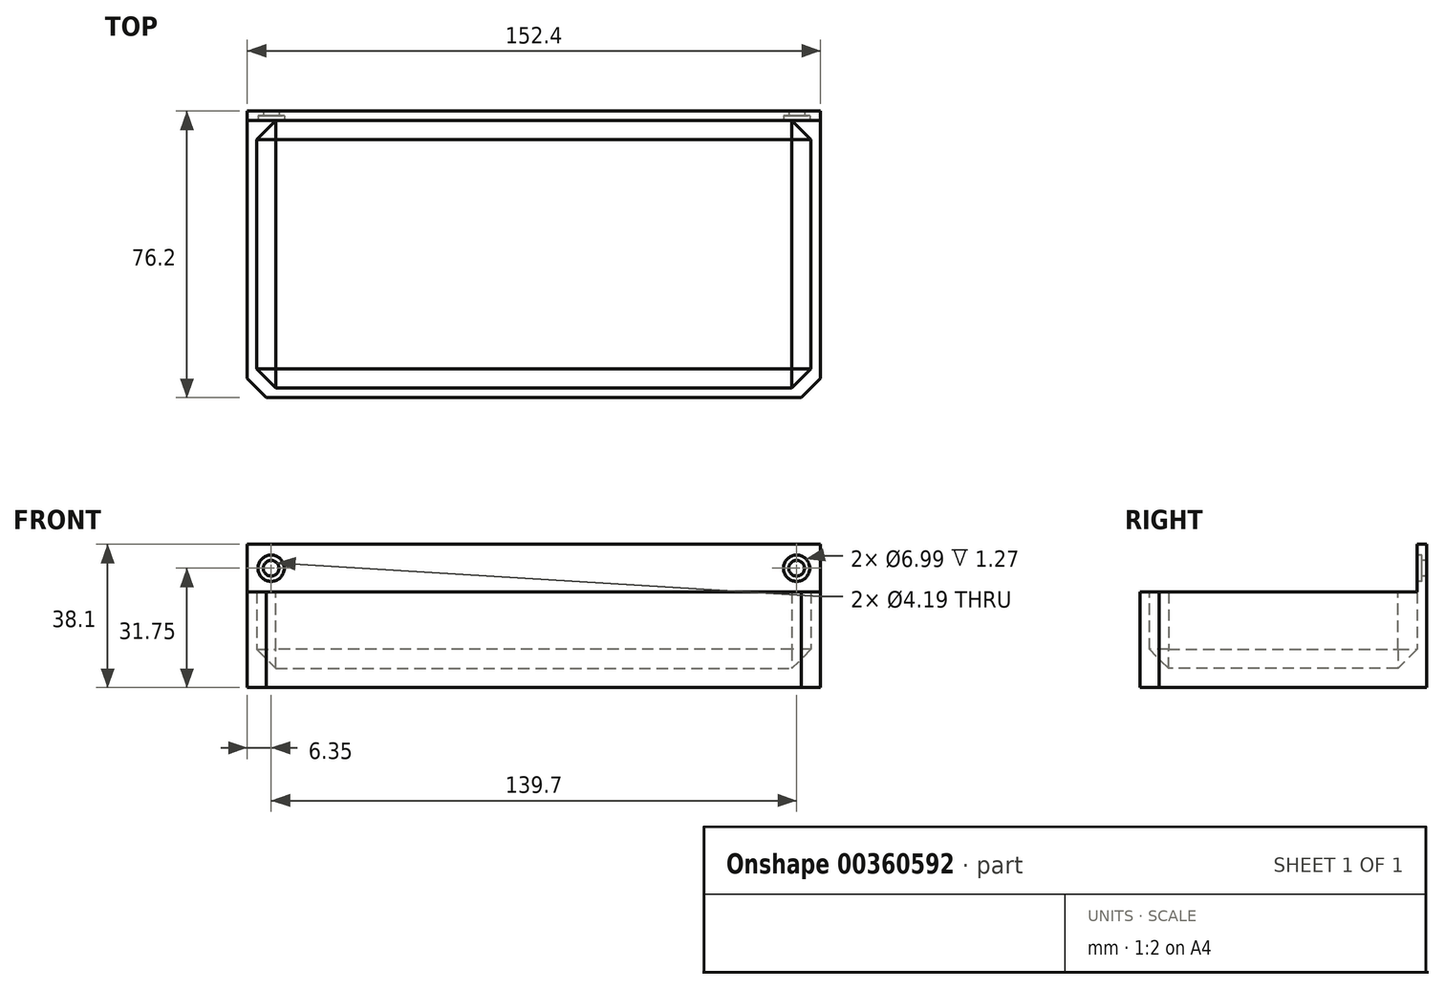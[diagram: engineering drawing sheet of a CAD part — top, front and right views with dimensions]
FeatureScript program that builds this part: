
annotation { "Feature Type Name" : "Feature", "Feature Type Description" : "" }
export const myFeature = defineFeature(function(context is Context, id is Id, definition is map)
    precondition{}
    {
        {
            var Q0;
            Q0=qCreatedBy(makeId("Top.planeOp"),FACE);
            var sketch = newSketch(context, id + "F0", { "sketchPlane" : qUnion([Q0])});
            skLineSegment(sketch, "E0.bottom", {"start": v(0, 0) * mm, "end": v(152.4, 0) * mm});
            skLineSegment(sketch, "E0.top", {"start": v(0, 76.2) * mm, "end": v(152.4, 76.2) * mm});
            skLineSegment(sketch, "E0.left", {"start": v(0, 0) * mm, "end": v(0, 76.2) * mm});
            skLineSegment(sketch, "E0.right", {"start": v(152.4, 0) * mm, "end": v(152.4, 76.2) * mm});
            skLineSegment(sketch, "E1.bottom", {"start": v(2.54, 2.54) * mm, "end": v(149.86, 2.54) * mm});
            skLineSegment(sketch, "E1.top", {"start": v(2.54, 73.66) * mm, "end": v(149.86, 73.66) * mm});
            skLineSegment(sketch, "E1.left", {"start": v(2.54, 2.54) * mm, "end": v(2.54, 73.66) * mm});
            skLineSegment(sketch, "E1.right", {"start": v(149.86, 2.54) * mm, "end": v(149.86, 73.66) * mm});
            skSolve(sketch);
        }
        {
            var Q0;
            Q0 = qSketchRegion(id + "F0", true);
            extrude(context, id + "F1", {"entities" : qUnion([Q0]), "depth" : 25.4 * mm});
        }
        {
            var Q0;
            Q0 = qSketchRegion(id + "F0", true);
            var Q1;
            Q1=makeQuery(id+"F0.imprint","IMPRINT",FACE,{"disambiguationData":[TD([[makeQuery(id+"F0.imprint","IMPRINT",EDGE,{"derivedFrom":sQuery(id+"F0.wireOp",EDGE,"E1.bottom")}),1.0]])]});
            extrude(context, id + "F2", {"entities" : qUnion([Q0, Q1]), "operationType" : NewBodyOperationType.ADD, "depth" : 5.08 * mm});
        }
        {
            var Q0;
            Q0=makeQuery(id+"F1.opExtrude","CAP_FACE",FACE,{"disambiguationData":[OSD([sQuery(id+"F0.wireOp",EDGE,"E0.bottom"),sQuery(id+"F0.wireOp",EDGE,"E0.top"),sQuery(id+"F0.wireOp",EDGE,"E0.left"),sQuery(id+"F0.wireOp",EDGE,"E0.right"),sQuery(id+"F0.wireOp",EDGE,"E1.bottom"),sQuery(id+"F0.wireOp",EDGE,"E1.top"),sQuery(id+"F0.wireOp",EDGE,"E1.left"),sQuery(id+"F0.wireOp",EDGE,"E1.right")])],"isStart":false});
            var sketch = newSketch(context, id + "F3", { "sketchPlane" : qUnion([Q0])});
            skLineSegment(sketch, "E2", {"start": v(0, 73.66) * mm, "end": v(152.4, 73.66) * mm});
            skSolve(sketch);
        }
        {
            var Q0;
            {var subQ0=makeQuery(id+"F1.opExtrude","CAP_EDGE",EDGE,{"disambiguationData":[OSD([sQuery(id+"F0.wireOp",EDGE,"E0.top")])],"isStart":false});Q0=makeQuery(id+"F3.imprint","IMPRINT",FACE,{"disambiguationData":[TD([[makeQuery(id+"F3.imprint","IMPRINT",EDGE,{"derivedFrom":subQ0}),-1.0]])]});}
            extrude(context, id + "F4", {"entities" : qUnion([Q0]), "operationType" : NewBodyOperationType.ADD, "depth" : 12.7 * mm});
        }
        {
            var Q0;
            Q0=makeQuery(id+"F4.boolean.opBoolean","MERGE",FACE,{"derivedFrom":[makeQuery(id+"F1.opExtrude","SWEPT_FACE",FACE,{"disambiguationData":[OSD([sQuery(id+"F0.wireOp",EDGE,"E1.top")])]}),makeQuery(id+"F4.opExtrude","SWEPT_FACE",FACE,{"disambiguationData":[OSD([sQuery(id+"F3.wireOp",EDGE,"E2")])]})]});
            var sketch = newSketch(context, id + "F5", { "sketchPlane" : qUnion([Q0])});
            skLineSegment(sketch, "E3", {"start": v(2.54, 25.4) * mm, "end": v(149.86, 25.4) * mm, "construction": true});
            skLineSegment(sketch, "E4", {"start": v(0, 31.75) * mm, "end": v(152.4, 31.75) * mm, "construction": true});
            skCircle(sketch, "E5", {"center": v(6.35, 31.75) * mm, "radius": 2.1 * mm});
            skCircle(sketch, "E6", {"center": v(6.35, 31.75) * mm, "radius": 3.5 * mm});
            skCircle(sketch, "E7", {"center": v(146.05, 31.75) * mm, "radius": 2.1 * mm});
            skCircle(sketch, "E8", {"center": v(146.05, 31.75) * mm, "radius": 3.5 * mm});
            skSolve(sketch);
        }
        {
            var Q0;
            Q0 = qSketchRegion(id + "F5", true);
            extrude(context, id + "F6", {"entities" : qUnion([Q0]), "operationType" : NewBodyOperationType.REMOVE, "oppositeDirection" : true, "depth" : 1.27 * mm});
        }
        {
            var Q0;
            Q0=makeQuery(id+"F6.boolean.opBoolean","SPLIT",FACE,{"disambiguationData":[TD([makeQuery(id+"F6.opExtrude","SWEPT_FACE",FACE,{"disambiguationData":[OSD([sQuery(id+"F5.wireOp",EDGE,"E5")])]})])],"derivedFrom":makeQuery(id+"F4.boolean.opBoolean","MERGE",FACE,{"derivedFrom":[makeQuery(id+"F1.opExtrude","SWEPT_FACE",FACE,{"disambiguationData":[OSD([sQuery(id+"F0.wireOp",EDGE,"E1.top")])]}),makeQuery(id+"F4.opExtrude","SWEPT_FACE",FACE,{"disambiguationData":[OSD([sQuery(id+"F3.wireOp",EDGE,"E2")])]})]})});
            var Q1;
            Q1=makeQuery(id+"F6.boolean.opBoolean","SPLIT",FACE,{"disambiguationData":[TD([makeQuery(id+"F6.opExtrude","SWEPT_FACE",FACE,{"disambiguationData":[OSD([sQuery(id+"F5.wireOp",EDGE,"E7")])]})])],"derivedFrom":makeQuery(id+"F4.boolean.opBoolean","MERGE",FACE,{"derivedFrom":[makeQuery(id+"F1.opExtrude","SWEPT_FACE",FACE,{"disambiguationData":[OSD([sQuery(id+"F0.wireOp",EDGE,"E1.top")])]}),makeQuery(id+"F4.opExtrude","SWEPT_FACE",FACE,{"disambiguationData":[OSD([sQuery(id+"F3.wireOp",EDGE,"E2")])]})]})});
            extrude(context, id + "F7", {"entities" : qUnion([Q0, Q1]), "operationType" : NewBodyOperationType.REMOVE, "oppositeDirection" : true, "depth" : 25.4 * mm});
        }
        {
            var Q0;
            Q0=makeQuery(id+"F1.opExtrude","SWEPT_EDGE",EDGE,{"disambiguationData":[OSD([sQuery(id+"F0.wireOp",EDGE,"E1.top"),sQuery(id+"F0.wireOp",EDGE,"E1.left")])]});
            var Q1;
            Q1=makeQuery(id+"F2.boolean.opBoolean","INTERSECT",EDGE,{"derivedFrom":[makeQuery(id+"F1.opExtrude","SWEPT_FACE",FACE,{"disambiguationData":[OSD([sQuery(id+"F0.wireOp",EDGE,"E1.top")])]}),makeQuery(id+"F2.opExtrude","CAP_FACE",FACE,{"disambiguationData":[OSD([sQuery(id+"F0.wireOp",EDGE,"E0.bottom"),sQuery(id+"F0.wireOp",EDGE,"E0.top"),sQuery(id+"F0.wireOp",EDGE,"E0.left"),sQuery(id+"F0.wireOp",EDGE,"E0.right")])],"isStart":false})]});
            var Q2;
            Q2=makeQuery(id+"F2.boolean.opBoolean","INTERSECT",EDGE,{"derivedFrom":[makeQuery(id+"F1.opExtrude","SWEPT_FACE",FACE,{"disambiguationData":[OSD([sQuery(id+"F0.wireOp",EDGE,"E1.left")])]}),makeQuery(id+"F2.opExtrude","CAP_FACE",FACE,{"disambiguationData":[OSD([sQuery(id+"F0.wireOp",EDGE,"E0.bottom"),sQuery(id+"F0.wireOp",EDGE,"E0.top"),sQuery(id+"F0.wireOp",EDGE,"E0.left"),sQuery(id+"F0.wireOp",EDGE,"E0.right")])],"isStart":false})]});
            var Q3;
            Q3=makeQuery(id+"F2.boolean.opBoolean","INTERSECT",EDGE,{"derivedFrom":[makeQuery(id+"F1.opExtrude","SWEPT_FACE",FACE,{"disambiguationData":[OSD([sQuery(id+"F0.wireOp",EDGE,"E1.bottom")])]}),makeQuery(id+"F2.opExtrude","CAP_FACE",FACE,{"disambiguationData":[OSD([sQuery(id+"F0.wireOp",EDGE,"E0.bottom"),sQuery(id+"F0.wireOp",EDGE,"E0.top"),sQuery(id+"F0.wireOp",EDGE,"E0.left"),sQuery(id+"F0.wireOp",EDGE,"E0.right")])],"isStart":false})]});
            var Q4;
            Q4=makeQuery(id+"F2.boolean.opBoolean","INTERSECT",EDGE,{"derivedFrom":[makeQuery(id+"F1.opExtrude","SWEPT_FACE",FACE,{"disambiguationData":[OSD([sQuery(id+"F0.wireOp",EDGE,"E1.right")])]}),makeQuery(id+"F2.opExtrude","CAP_FACE",FACE,{"disambiguationData":[OSD([sQuery(id+"F0.wireOp",EDGE,"E0.bottom"),sQuery(id+"F0.wireOp",EDGE,"E0.top"),sQuery(id+"F0.wireOp",EDGE,"E0.left"),sQuery(id+"F0.wireOp",EDGE,"E0.right")])],"isStart":false})]});
            var Q5;
            Q5=makeQuery(id+"F1.opExtrude","SWEPT_EDGE",EDGE,{"disambiguationData":[OSD([sQuery(id+"F0.wireOp",EDGE,"E1.bottom"),sQuery(id+"F0.wireOp",EDGE,"E1.left")])]});
            var Q6;
            Q6=makeQuery(id+"F1.opExtrude","SWEPT_EDGE",EDGE,{"disambiguationData":[OSD([sQuery(id+"F0.wireOp",EDGE,"E1.bottom"),sQuery(id+"F0.wireOp",EDGE,"E1.right")])]});
            var Q7;
            Q7=makeQuery(id+"F1.opExtrude","SWEPT_EDGE",EDGE,{"disambiguationData":[OSD([sQuery(id+"F0.wireOp",EDGE,"E1.top"),sQuery(id+"F0.wireOp",EDGE,"E1.right")])]});
            var Q8;
            Q8=makeQuery(id+"F1.opExtrude","SWEPT_EDGE",EDGE,{"disambiguationData":[OSD([sQuery(id+"F0.wireOp",EDGE,"E0.bottom"),sQuery(id+"F0.wireOp",EDGE,"E0.left")])]});
            var Q9;
            Q9=makeQuery(id+"F1.opExtrude","SWEPT_EDGE",EDGE,{"disambiguationData":[OSD([sQuery(id+"F0.wireOp",EDGE,"E0.bottom"),sQuery(id+"F0.wireOp",EDGE,"E0.right")])]});
            chamfer(context, id + "F8", {"entities" : qUnion([Q0, Q1, Q2, Q3, Q4, Q5, Q6, Q7, Q8, Q9]), "width" : 5.08 * mm, "tangentPropagation" : true});
        }
    });
